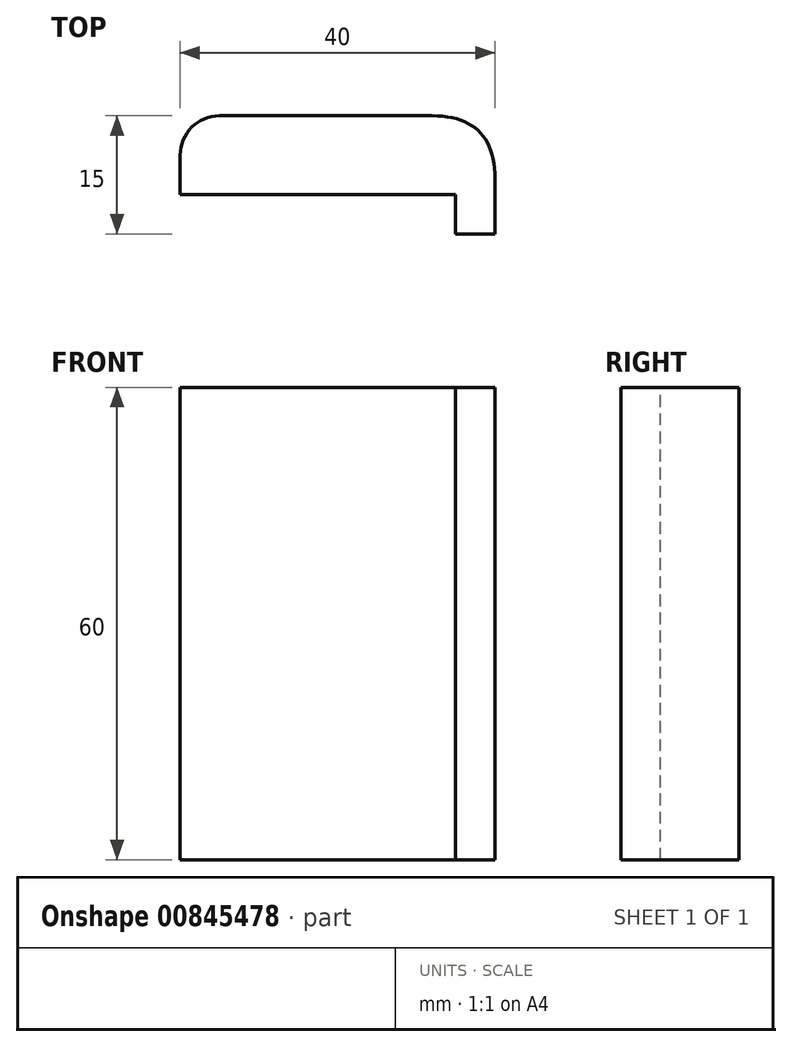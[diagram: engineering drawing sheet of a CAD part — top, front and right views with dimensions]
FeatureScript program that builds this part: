
annotation { "Feature Type Name" : "Feature", "Feature Type Description" : "" }
export const myFeature = defineFeature(function(context is Context, id is Id, definition is map)
    precondition{}
    {
        {
            var Q0;
            Q0=qCreatedBy(makeId("Top.planeOp"),FACE);
            var sketch = newSketch(context, id + "F0", { "sketchPlane" : qUnion([Q0])});
            skLineSegment(sketch, "E0.bottom", {"start": v(0, 0) * mm, "end": v(40, 0) * mm});
            skLineSegment(sketch, "E0.top", {"start": v(0, -15) * mm, "end": v(40, -15) * mm});
            skLineSegment(sketch, "E0.left", {"start": v(0, 0) * mm, "end": v(0, -15) * mm});
            skLineSegment(sketch, "E0.right", {"start": v(40, 0) * mm, "end": v(40, -15) * mm});
            skSolve(sketch);
        }
        {
            var Q0;
            Q0 = qSketchRegion(id + "F0", true);
            extrude(context, id + "F1", {"entities" : qUnion([Q0]), "depth" : 60 * mm, "offsetDistance" : 25.4 * mm});
        }
        {
            var Q0;
            Q0=makeQuery(id+"F1.opExtrude","CAP_FACE",FACE,{"disambiguationData":[OSD([sQuery(id+"F0.wireOp",EDGE,"E0.bottom"),sQuery(id+"F0.wireOp",EDGE,"E0.top"),sQuery(id+"F0.wireOp",EDGE,"E0.left"),sQuery(id+"F0.wireOp",EDGE,"E0.right")])],"isStart":false});
            var sketch = newSketch(context, id + "F2", { "sketchPlane" : qUnion([Q0])});
            skLineSegment(sketch, "E1.bottom", {"start": v(0, -15) * mm, "end": v(35, -15) * mm});
            skLineSegment(sketch, "E1.top", {"start": v(0, -10) * mm, "end": v(35, -10) * mm});
            skLineSegment(sketch, "E1.left", {"start": v(0, -15) * mm, "end": v(0, -10) * mm});
            skLineSegment(sketch, "E1.right", {"start": v(35, -15) * mm, "end": v(35, -10) * mm});
            skSolve(sketch);
        }
        {
            var Q0;
            Q0 = qSketchRegion(id + "F2", true);
            var Q1;
            Q1=makeQuery(id+"F1.opExtrude","CAP_FACE",FACE,{"disambiguationData":[OSD([sQuery(id+"F0.wireOp",EDGE,"E0.bottom"),sQuery(id+"F0.wireOp",EDGE,"E0.top"),sQuery(id+"F0.wireOp",EDGE,"E0.left"),sQuery(id+"F0.wireOp",EDGE,"E0.right")])],"isStart":true});
            extrude(context, id + "F3", {"entities" : qUnion([Q0]), "operationType" : NewBodyOperationType.REMOVE, "endBound" : BoundingType.UP_TO_SURFACE, "oppositeDirection" : true, "depth" : 25 * mm, "endBoundEntityFace" : qUnion([Q1]), "offsetDistance" : 25 * mm});
        }
        {
            var Q0;
            Q0=makeQuery(id+"F1.opExtrude","SWEPT_EDGE",EDGE,{"disambiguationData":[OSD([sQuery(id+"F0.wireOp",EDGE,"E0.bottom"),sQuery(id+"F0.wireOp",EDGE,"E0.right")])]});
            fillet(context, id + "F4", {"entities" : qUnion([Q0]), "radius" : 8 * mm, "tangentPropagation" : true, "rho" : 0.5, "crossSection" : FilletCrossSection.CONIC, "allowEdgeOverflow" : false});
        }
        {
            var Q0;
            Q0=makeQuery(id+"F1.opExtrude","SWEPT_EDGE",EDGE,{"disambiguationData":[OSD([sQuery(id+"F0.wireOp",EDGE,"E0.bottom"),sQuery(id+"F0.wireOp",EDGE,"E0.left")])]});
            fillet(context, id + "F5", {"entities" : qUnion([Q0]), "radius" : 5 * mm, "tangentPropagation" : true, "allowEdgeOverflow" : false});
        }
    });
